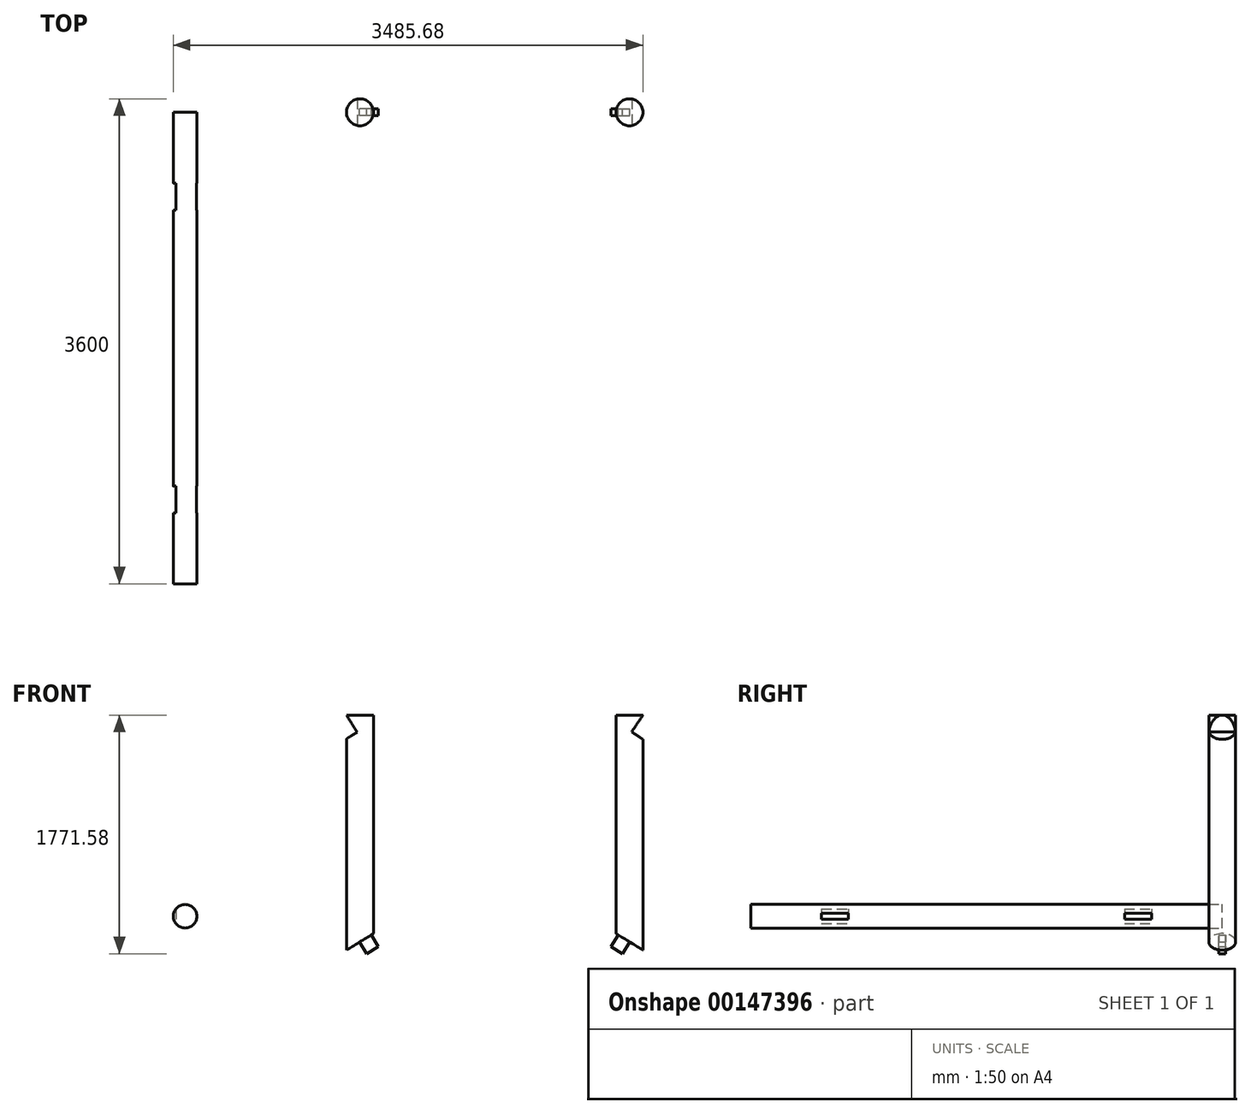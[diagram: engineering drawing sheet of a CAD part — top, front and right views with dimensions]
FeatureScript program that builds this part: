
annotation { "Feature Type Name" : "Feature", "Feature Type Description" : "" }
export const myFeature = defineFeature(function(context is Context, id is Id, definition is map)
    precondition{}
    {
        {
            var Q0;
            Q0=qCreatedBy(makeId("Top.planeOp"),FACE);
            var sketch = newSketch(context, id + "F0", { "sketchPlane" : qUnion([Q0])});
            skCircle(sketch, "E0", {"center": v(0, 0) * mm, "radius": 100 * mm});
            skSolve(sketch);
        }
        {
            var Q0;
            Q0 = qSketchRegion(id + "F0", true);
            extrude(context, id + "F1", {"entities" : qUnion([Q0]), "depth" : 1757 * mm});
        }
        {
            var Q0;
            Q0=qCreatedBy(makeId("Front.planeOp"),FACE);
            var sketch = newSketch(context, id + "F2", { "sketchPlane" : qUnion([Q0])});
            skLineSegment(sketch, "E1", {"start": v(-218.33, -60.52) * mm, "end": v(187.26, 189.2) * mm});
            skLineSegment(sketch, "E2", {"start": v(187.26, 189.2) * mm, "end": v(187.26, -60.52) * mm});
            skLineSegment(sketch, "E3", {"start": v(187.26, -60.52) * mm, "end": v(-218.33, -60.52) * mm});
            skSolve(sketch);
        }
        {
            var Q0;
            Q0 = qSketchRegion(id + "F2", true);
            extrude(context, id + "F3", {"entities" : qUnion([Q0]), "operationType" : NewBodyOperationType.REMOVE, "endBound" : BoundingType.SYMMETRIC, "oppositeDirection" : true, "depth" : 200 * mm});
        }
        {
            var Q0;
            Q0=makeQuery(id+"F3.boolean.opBoolean","COPY",FACE,{"derivedFrom":makeQuery(id+"F3.opExtrude","SWEPT_FACE",FACE,{"disambiguationData":[OSD([sQuery(id+"F2.wireOp",EDGE,"E1")])]})});
            var sketch = newSketch(context, id + "F4", { "sketchPlane" : qUnion([Q0])});
            skLineSegment(sketch, "E4", {"start": v(194.82, 0) * mm, "end": v(-160.7, 0) * mm, "construction": true});
            skLineSegment(sketch, "E5.bottom", {"start": v(136.6, 25.4) * mm, "end": v(35, 25.4) * mm});
            skLineSegment(sketch, "E5.top", {"start": v(136.6, -25.4) * mm, "end": v(35, -25.4) * mm});
            skLineSegment(sketch, "E5.left", {"start": v(136.6, 25.4) * mm, "end": v(136.6, -25.4) * mm});
            skLineSegment(sketch, "E5.right", {"start": v(35, 25.4) * mm, "end": v(35, -25.4) * mm});
            skSolve(sketch);
        }
        {
            var Q0;
            Q0 = qSketchRegion(id + "F4", true);
            extrude(context, id + "F5", {"entities" : qUnion([Q0]), "operationType" : NewBodyOperationType.ADD, "depth" : 101.6 * mm});
        }
        {
            var Q0;
            Q0=qCreatedBy(makeId("Right.planeOp"),FACE);
            cPlane(context, id + "F6", {"entities" : qUnion([Q0]), "cplaneType" : CPlaneType.OFFSET, "offset" : 1000 * mm, "width" : 150 * mm, "height" : 150 * mm});
        }
        {
            var Q0;
            Q0=makeQuery(id+"F1.opExtrude","SWEPT_BODY",BODY,{"disambiguationData":[OSD([sQuery(id+"F0.wireOp",EDGE,"E0")])]});
            var Q1;
            Q1=qCreatedBy(id+"F6.planeOp",FACE);
            mirror(context, id + "F7", {"entities" : qUnion([Q0]), "mirrorPlane" : qUnion([Q1])});
        }
        {
            var Q0;
            Q0=qCreatedBy(makeId("Front.planeOp"),FACE);
            var sketch = newSketch(context, id + "F8", { "sketchPlane" : qUnion([Q0])});
            skCircle(sketch, "E6", {"center": v(-1298.18, 263.47) * mm, "radius": 87.5 * mm});
            skSolve(sketch);
        }
        {
            var Q0;
            Q0 = qSketchRegion(id + "F8", true);
            extrude(context, id + "F9", {"entities" : qUnion([Q0]), "depth" : 3500 * mm});
        }
        {
            var Q0;
            Q0=qCreatedBy(makeId("Front.planeOp"),FACE);
            var sketch = newSketch(context, id + "F10", { "sketchPlane" : qUnion([Q0])});
            skLineSegment(sketch, "E7.0", {"start": v(1580.8, 927.86) * mm, "end": v(-46.73, -74.19) * mm, "construction": true});
            skLineSegment(sketch, "E8.0", {"start": v(-100, 1757) * mm, "end": v(100, 1757) * mm, "construction": true});
            skLineSegment(sketch, "E9", {"start": v(-100, 1757) * mm, "end": v(732.17, 405.38) * mm, "construction": true});
            skLineSegment(sketch, "E10", {"start": v(-100, 1757) * mm, "end": v(-21.36, 1629.27) * mm});
            skLineSegment(sketch, "E11", {"start": v(-21.36, 1629.27) * mm, "end": v(-106.51, 1576.84) * mm});
            skLineSegment(sketch, "E12", {"start": v(-106.51, 1576.84) * mm, "end": v(-100, 1757) * mm});
            skSolve(sketch);
        }
        {
            var Q0;
            Q0 = qSketchRegion(id + "F10", true);
            extrude(context, id + "F11", {"entities" : qUnion([Q0]), "operationType" : NewBodyOperationType.REMOVE, "endBound" : BoundingType.SYMMETRIC, "oppositeDirection" : true, "depth" : 200 * mm});
        }
        {
            var Q0;
            Q0=qCreatedBy(makeId("Front.planeOp"),FACE);
            var sketch = newSketch(context, id + "F12", { "sketchPlane" : qUnion([Q0])});
            skLineSegment(sketch, "E13.0", {"start": v(595.76, 819.16) * mm, "end": v(2046.73, -74.19) * mm, "construction": true});
            skLineSegment(sketch, "E14.0", {"start": v(2100, 1757) * mm, "end": v(1900, 1757) * mm});
            skLineSegment(sketch, "E15", {"start": v(2100, 1757) * mm, "end": v(2016.8, 1632.2) * mm});
            skLineSegment(sketch, "E16", {"start": v(2016.8, 1632.2) * mm, "end": v(2100, 1576.72) * mm});
            skLineSegment(sketch, "E17", {"start": v(2100, 1757) * mm, "end": v(2100, 1576.72) * mm});
            skSolve(sketch);
        }
        {
            var Q0;
            Q0 = qSketchRegion(id + "F12", true);
            extrude(context, id + "F13", {"entities" : qUnion([Q0]), "operationType" : NewBodyOperationType.REMOVE, "endBound" : BoundingType.SYMMETRIC, "oppositeDirection" : true, "depth" : 200 * mm});
        }
        {
            var Q0;
            Q0=qCreatedBy(makeId("Top.planeOp"),FACE);
            var sketch = newSketch(context, id + "F14", { "sketchPlane" : qUnion([Q0])});
            skLineSegment(sketch, "E18", {"start": v(-1931.13, 0) * mm, "end": v(-650.1, 0) * mm, "construction": true});
            skLineSegment(sketch, "E19.0", {"start": v(-1931.13, -625.5) * mm, "end": v(-650.1, -625.5) * mm, "construction": true});
            skLineSegment(sketch, "E20.0", {"start": v(-1931.13, -3500) * mm, "end": v(-650.1, -3500) * mm, "construction": true});
            skLineSegment(sketch, "E21.0", {"start": v(-1931.13, -2874.5) * mm, "end": v(-650.1, -2874.5) * mm, "construction": true});
            skLineSegment(sketch, "E22.0", {"start": v(-1931.13, -725.5) * mm, "end": v(-650.1, -725.5) * mm, "construction": true});
            skLineSegment(sketch, "E23.0", {"start": v(-1931.13, -525.5) * mm, "end": v(-650.1, -525.5) * mm, "construction": true});
            skLineSegment(sketch, "E24.0", {"start": v(-1931.13, -2974.5) * mm, "end": v(-650.1, -2974.5) * mm, "construction": true});
            skLineSegment(sketch, "E25.0", {"start": v(-1931.13, -2774.5) * mm, "end": v(-650.1, -2774.5) * mm, "construction": true});
            skLineSegment(sketch, "E26", {"start": v(-1290.6, -28.2) * mm, "end": v(-1290.6, -3887.39) * mm, "construction": true});
            skPoint(sketch, "E26.startSnap0", {"position": v(-1290.6, 0) * mm});
            skLineSegment(sketch, "E27.0", {"start": v(-1367.6, -28.2) * mm, "end": v(-1367.6, -3887.39) * mm, "construction": true});
            skLineSegment(sketch, "E28.0", {"start": v(-1213.6, -28.2) * mm, "end": v(-1213.6, -3887.39) * mm, "construction": true});
            skLineSegment(sketch, "E29.bottom", {"start": v(-1213.6, -525.5) * mm, "end": v(-1166.28, -525.5) * mm});
            skLineSegment(sketch, "E29.top", {"start": v(-1213.6, -725.5) * mm, "end": v(-1166.28, -725.5) * mm});
            skLineSegment(sketch, "E29.left", {"start": v(-1213.6, -525.5) * mm, "end": v(-1213.6, -725.5) * mm});
            skLineSegment(sketch, "E29.right", {"start": v(-1166.28, -525.5) * mm, "end": v(-1166.28, -725.5) * mm});
            skLineSegment(sketch, "E30.bottom", {"start": v(-1367.6, -525.5) * mm, "end": v(-1419.28, -525.5) * mm});
            skLineSegment(sketch, "E30.top", {"start": v(-1367.6, -725.5) * mm, "end": v(-1419.28, -725.5) * mm});
            skLineSegment(sketch, "E30.left", {"start": v(-1367.6, -525.5) * mm, "end": v(-1367.6, -725.5) * mm});
            skLineSegment(sketch, "E30.right", {"start": v(-1419.28, -525.5) * mm, "end": v(-1419.28, -725.5) * mm});
            skLineSegment(sketch, "E31.bottom", {"start": v(-1213.6, -2774.5) * mm, "end": v(-1165.13, -2774.5) * mm});
            skLineSegment(sketch, "E31.top", {"start": v(-1213.6, -2974.5) * mm, "end": v(-1165.13, -2974.5) * mm});
            skLineSegment(sketch, "E31.left", {"start": v(-1213.6, -2774.5) * mm, "end": v(-1213.6, -2974.5) * mm});
            skLineSegment(sketch, "E31.right", {"start": v(-1165.13, -2774.5) * mm, "end": v(-1165.13, -2974.5) * mm});
            skLineSegment(sketch, "E32.bottom", {"start": v(-1367.6, -2774.5) * mm, "end": v(-1415.41, -2774.5) * mm});
            skLineSegment(sketch, "E32.top", {"start": v(-1367.6, -2974.5) * mm, "end": v(-1415.41, -2974.5) * mm});
            skLineSegment(sketch, "E32.left", {"start": v(-1367.6, -2774.5) * mm, "end": v(-1367.6, -2974.5) * mm});
            skLineSegment(sketch, "E32.right", {"start": v(-1415.41, -2774.5) * mm, "end": v(-1415.41, -2974.5) * mm});
            skSolve(sketch);
        }
        {
            var Q0;
            Q0 = qSketchRegion(id + "F14", true);
            extrude(context, id + "F15", {"entities" : qUnion([Q0]), "operationType" : NewBodyOperationType.REMOVE, "endBound" : BoundingType.THROUGH_ALL, "depth" : 25 * mm});
        }
    });
